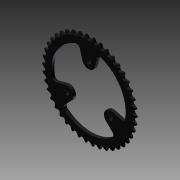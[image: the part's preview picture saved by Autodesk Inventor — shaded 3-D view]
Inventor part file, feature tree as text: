
AUTODESK INVENTOR PART (.ipt)
format: ipt  version: 2012 (Build 160160000, 160)  size: 1,149,440 bytes
history: native  units: in
note: dims shown in document units (in); Inventor stores cm internally (conversion verified against a paired STEP export)
features: boolean_combine x1, extrude x1, fillet x1, imported_body x1, sketch x1
ambient origin geometry x8: Origin, YZ Plane, XZ Plane, XY Plane, X Axis, Y Axis, Z Axis, Center Point
feature tree (5):
  boolean_combine  "Combine1"
  extrude  "Extrusion1"  TaperAngle=0.0deg  [1 undecoded]
  fillet  "Fillet1"  Radius=0.125in
  imported_body  "Base1"
  sketch  "Sketch1"  dims[d0=1.375in d1=0.0in d2=0.0in d3=0.125in]
note: 1 required parameter value undecoded (feature->parameter linkage not recoverable at this tier; creation-order binding heuristic only, values carry confidence <= 0.55)
